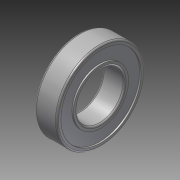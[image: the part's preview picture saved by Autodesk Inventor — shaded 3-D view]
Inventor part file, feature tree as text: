
AUTODESK INVENTOR PART (.ipt)
format: ipt  version: 2014 SP1 (Build 180222100, 222)  size: 151,552 bytes
history: native  units: in
note: dims shown in document units (in); Inventor stores cm internally (conversion verified against a paired STEP export)
features: fillet x1, other x1, imported_body x1
ambient origin geometry x8: Origin, YZ Plane, XZ Plane, XY Plane, X Axis, Y Axis, Z Axis, Center Point
bodies: Body1 (feature_tree)
feature tree (3):
  fillet  "Fillet1"  [1 undecoded]
  other  "217-2742.ipt1"
  imported_body  "Base1"
note: 1 required parameter value undecoded (feature->parameter linkage not recoverable at this tier; creation-order binding heuristic only, values carry confidence <= 0.55)
